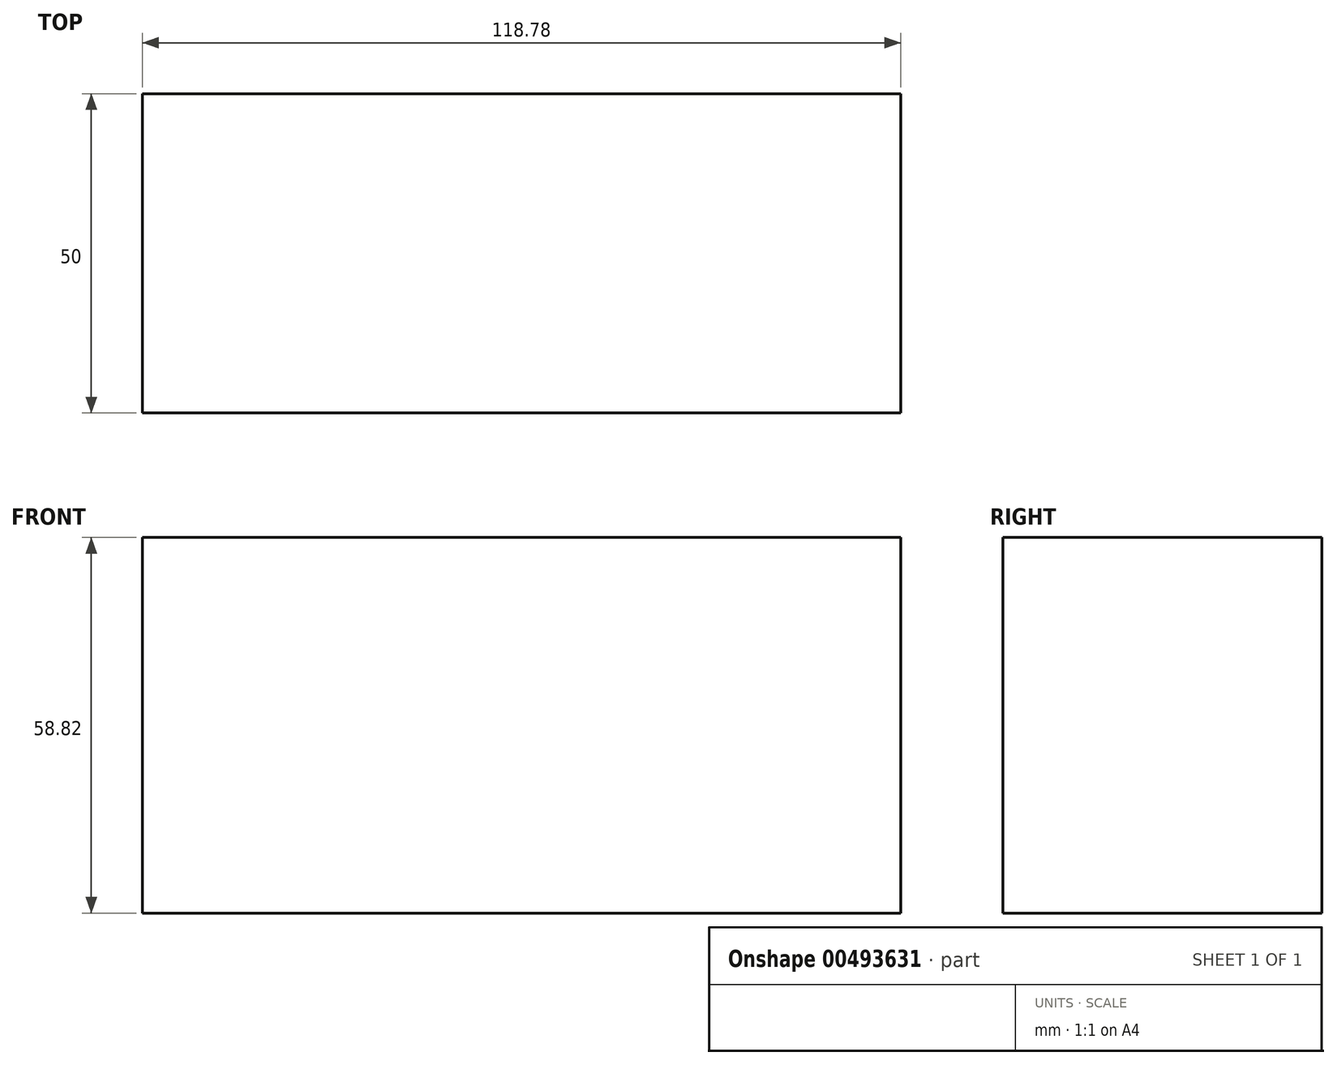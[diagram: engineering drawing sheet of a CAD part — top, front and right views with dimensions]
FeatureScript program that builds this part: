
annotation { "Feature Type Name" : "Feature", "Feature Type Description" : "" }
export const myFeature = defineFeature(function(context is Context, id is Id, definition is map)
    precondition{}
    {
        {
            var Q0;
            Q0=qCreatedBy(makeId("Front.planeOp"),FACE);
            var sketch = newSketch(context, id + "F0", { "sketchPlane" : qUnion([Q0])});
            skLineSegment(sketch, "E0.bottom", {"start": v(59.39, 29.4) * mm, "end": v(-59.39, 29.4) * mm});
            skLineSegment(sketch, "E0.top", {"start": v(59.39, -29.4) * mm, "end": v(-59.39, -29.4) * mm});
            skLineSegment(sketch, "E0.left", {"start": v(59.39, 29.4) * mm, "end": v(59.39, -29.4) * mm});
            skLineSegment(sketch, "E0.right", {"start": v(-59.39, 29.4) * mm, "end": v(-59.39, -29.4) * mm});
            skPoint(sketch, "E0.middle", {"position": v(0, 0) * mm});
            skSolve(sketch);
        }
        {
            var Q0;
            Q0 = qSketchRegion(id + "F0", true);
            extrude(context, id + "F1", {"entities" : qUnion([Q0]), "depth" : 50 * mm});
        }
    });
